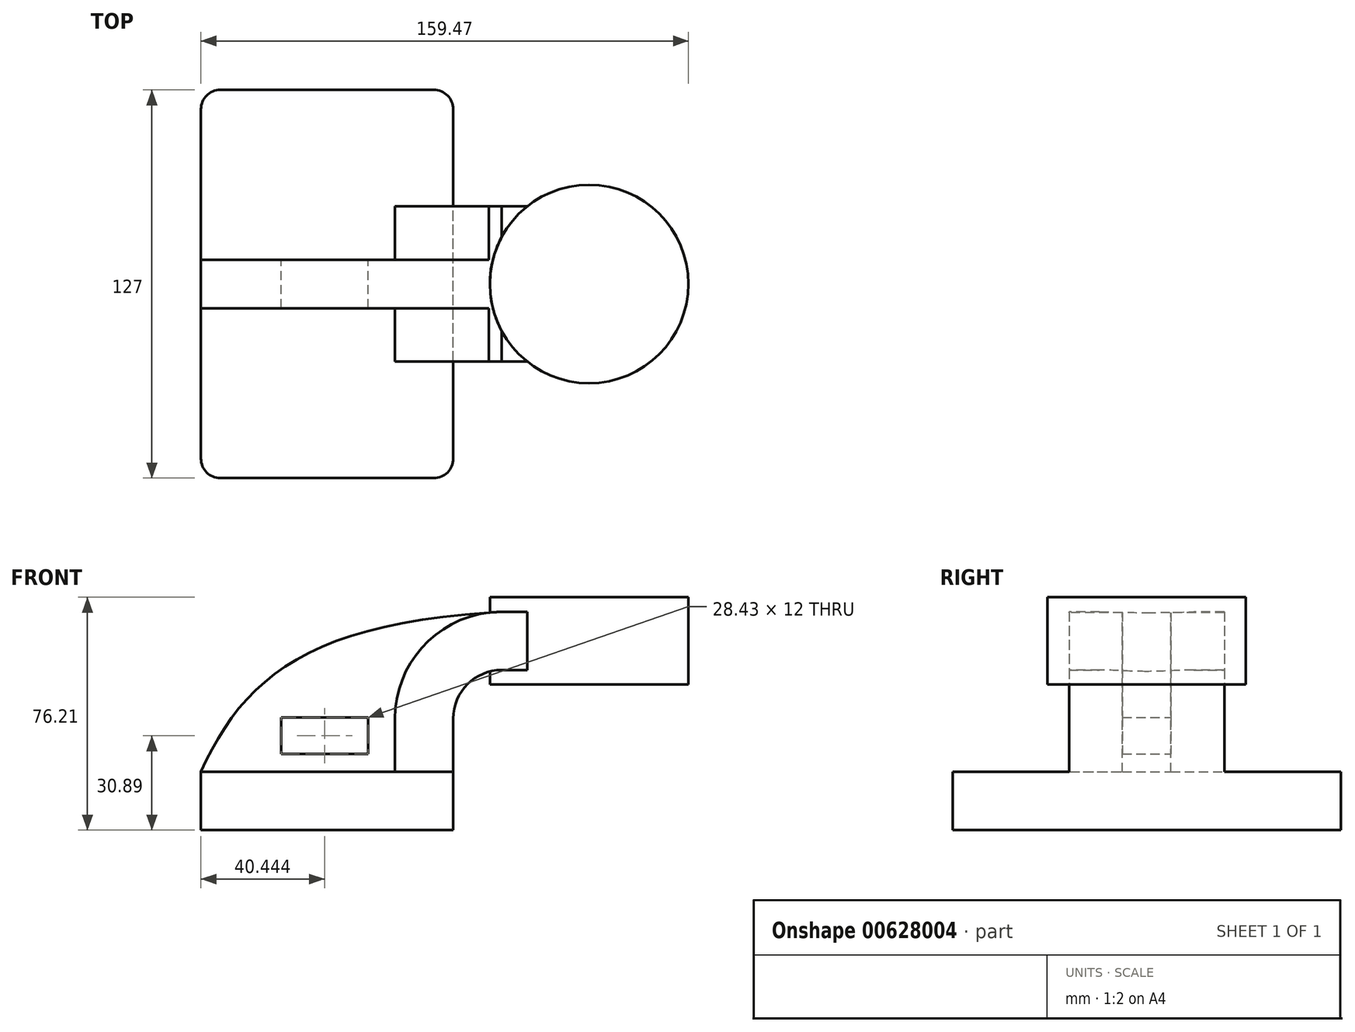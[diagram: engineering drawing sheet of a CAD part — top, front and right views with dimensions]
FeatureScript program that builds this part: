
annotation { "Feature Type Name" : "Feature", "Feature Type Description" : "" }
export const myFeature = defineFeature(function(context is Context, id is Id, definition is map)
    precondition{}
    {
        {
            var Q0;
            Q0=qCreatedBy(makeId("Front.planeOp"),FACE);
            var sketch = newSketch(context, id + "F0", { "sketchPlane" : qUnion([Q0])});
            skLineSegment(sketch, "E0.bottom", {"start": v(-41.27, -9.53) * mm, "end": v(41.28, -9.53) * mm});
            skLineSegment(sketch, "E0.top", {"start": v(-41.28, 9.53) * mm, "end": v(41.28, 9.53) * mm});
            skLineSegment(sketch, "E0.left", {"start": v(-41.28, -9.53) * mm, "end": v(-41.28, 9.53) * mm});
            skLineSegment(sketch, "E0.right", {"start": v(41.28, -9.53) * mm, "end": v(41.28, 9.52) * mm});
            skPoint(sketch, "E0.middle", {"position": v(0, 0) * mm});
            skLineSegment(sketch, "E1.bottom", {"start": v(118.2, 66.68) * mm, "end": v(67.4, 66.68) * mm});
            skLineSegment(sketch, "E1.top", {"start": v(118.2, 38.1) * mm, "end": v(67.4, 38.1) * mm});
            skLineSegment(sketch, "E1.left", {"start": v(118.2, 66.68) * mm, "end": v(118.2, 38.1) * mm});
            skLineSegment(sketch, "E1.right", {"start": v(67.4, 66.68) * mm, "end": v(67.4, 38.1) * mm});
            skLineSegment(sketch, "E2", {"start": v(41.28, 9.52) * mm, "end": v(41.28, 27) * mm});
            skArc(sketch, "E3", {"start": v(41.27, 27) * mm, "mid": v(45.92, 38.23) * mm, "end": v(57.15, 42.88) * mm});
            skLineSegment(sketch, "E4", {"start": v(57.15, 42.88) * mm, "end": v(85.72, 42.88) * mm});
            skLineSegment(sketch, "E5.0", {"start": v(57.15, 61.93) * mm, "end": v(85.72, 61.93) * mm});
            skArc(sketch, "E5.1", {"start": v(22.22, 27) * mm, "mid": v(32.45, 51.7) * mm, "end": v(57.15, 61.93) * mm});
            skLineSegment(sketch, "E5.2", {"start": v(22.22, 9.52) * mm, "end": v(22.22, 27) * mm});
            skFitSpline(sketch, "E6", {"points": [v(-41.28, 9.53) * mm, v(57.15, 61.93) * mm], "startDerivative": vector(41.15, 90.94) * mm, "endDerivative": vector(191.58, 10.57) * mm});
            skLineSegment(sketch, "E7", {"start": v(85.73, 42.88) * mm, "end": v(85.72, 61.93) * mm});
            skLineSegment(sketch, "E8", {"start": v(85.72, 42.88) * mm, "end": v(85.72, 38.1) * mm});
            skLineSegment(sketch, "E9", {"start": v(85.72, 38.1) * mm, "end": v(85.72, 61.93) * mm});
            skLineSegment(sketch, "E10", {"start": v(85.72, 66.68) * mm, "end": v(85.72, 61.93) * mm});
            skLineSegment(sketch, "E11.bottom", {"start": v(-15.05, 27.36) * mm, "end": v(13.38, 27.36) * mm});
            skLineSegment(sketch, "E11.top", {"start": v(-15.05, 15.36) * mm, "end": v(13.38, 15.36) * mm});
            skLineSegment(sketch, "E11.left", {"start": v(-15.05, 27.36) * mm, "end": v(-15.05, 15.36) * mm});
            skLineSegment(sketch, "E11.right", {"start": v(13.38, 27.36) * mm, "end": v(13.38, 15.36) * mm});
            skSolve(sketch);
        }
        {
            var Q0;
            Q0=makeQuery(id+"F0.imprint","IMPRINT",FACE,{"disambiguationData":[TD([[makeQuery(id+"F0.imprint","IMPRINT",EDGE,{"derivedFrom":sQuery(id+"F0.wireOp",EDGE,"E0.bottom")}),1.0]])]});
            extrude(context, id + "F1", {"entities" : qUnion([Q0]), "endBound" : BoundingType.SYMMETRIC, "depth" : 127 * mm, "offsetDistance" : 25.4 * mm});
        }
        {
            var Q0;
            {var subQ3=sQuery(id+"F0.wireOp",EDGE,"E5.2");Q0=makeQuery(id+"F0.imprint","IMPRINT",FACE,{"disambiguationData":[TD([[makeQuery(id+"F0.imprint","IMPRINT",EDGE,{"derivedFrom":subQ3}),1.0]])]});}
            extrude(context, id + "F2", {"entities" : qUnion([Q0]), "operationType" : NewBodyOperationType.ADD, "endBound" : BoundingType.SYMMETRIC, "depth" : 15.88 * mm, "offsetDistance" : 25.4 * mm});
        }
        {
            var Q0;
            {var subQ1=sQuery(id+"F0.wireOp",EDGE,"E2");Q0=makeQuery(id+"F0.imprint","IMPRINT",FACE,{"disambiguationData":[TD([[makeQuery(id+"F0.imprint","IMPRINT",EDGE,{"derivedFrom":subQ1}),1.0]])]});}
            var Q1;
            {var subQ0=sQuery(id+"F0.wireOp",EDGE,"E5.0");var subQ1=sQuery(id+"F0.wireOp",EDGE,"E1.right");var subQ2=makeQuery(id+"F0.imprint","INTERSECT",VERTEX,{"derivedFrom":[subQ1,subQ0]});Q1=makeQuery(id+"F0.imprint","IMPRINT",FACE,{"disambiguationData":[TD([[makeQuery(id+"F0.imprint","IMPRINT",EDGE,{"disambiguationData":[TD([[subQ2,-1.0]])],"derivedFrom":subQ1}),1.0]])]});}
            extrude(context, id + "F3", {"entities" : qUnion([Q0, Q1]), "operationType" : NewBodyOperationType.ADD, "endBound" : BoundingType.SYMMETRIC, "depth" : 50.8 * mm, "offsetDistance" : 25.4 * mm});
        }
        {
            var Q0;
            {var subQ4=sQuery(id+"F0.wireOp",EDGE,"E1.left");Q0=makeQuery(id+"F0.imprint","IMPRINT",FACE,{"disambiguationData":[TD([[makeQuery(id+"F0.imprint","IMPRINT",EDGE,{"derivedFrom":subQ4}),-1.0]])]});}
            var Q1;
            Q1=sQuery(id+"F0.wireOp",EDGE,"E7");
            revolve(context, id + "F4", {"operationType" : NewBodyOperationType.ADD, "entities" : qUnion([Q0]), "axis" : qUnion([Q1]), "revolveType" : RevolveType.FULL});
        }
        {
            var Q0;
            Q0=makeQuery(id+"F1.opExtrude","CAP_EDGE",EDGE,{"disambiguationData":[OSD([sQuery(id+"F0.wireOp",EDGE,"E0.left")])],"isStart":false});
            var Q1;
            Q1=makeQuery(id+"F1.opExtrude","CAP_EDGE",EDGE,{"disambiguationData":[OSD([sQuery(id+"F0.wireOp",EDGE,"E0.right")])],"isStart":false});
            var Q2;
            Q2=makeQuery(id+"F1.opExtrude","CAP_EDGE",EDGE,{"disambiguationData":[OSD([sQuery(id+"F0.wireOp",EDGE,"E0.right")])],"isStart":true});
            var Q3;
            Q3=makeQuery(id+"F1.opExtrude","CAP_EDGE",EDGE,{"disambiguationData":[OSD([sQuery(id+"F0.wireOp",EDGE,"E0.left")])],"isStart":true});
            fillet(context, id + "F5", {"entities" : qUnion([Q0, Q1, Q2, Q3]), "radius" : 6.35 * mm, "tangentPropagation" : true, "allowEdgeOverflow" : false});
        }
    });
